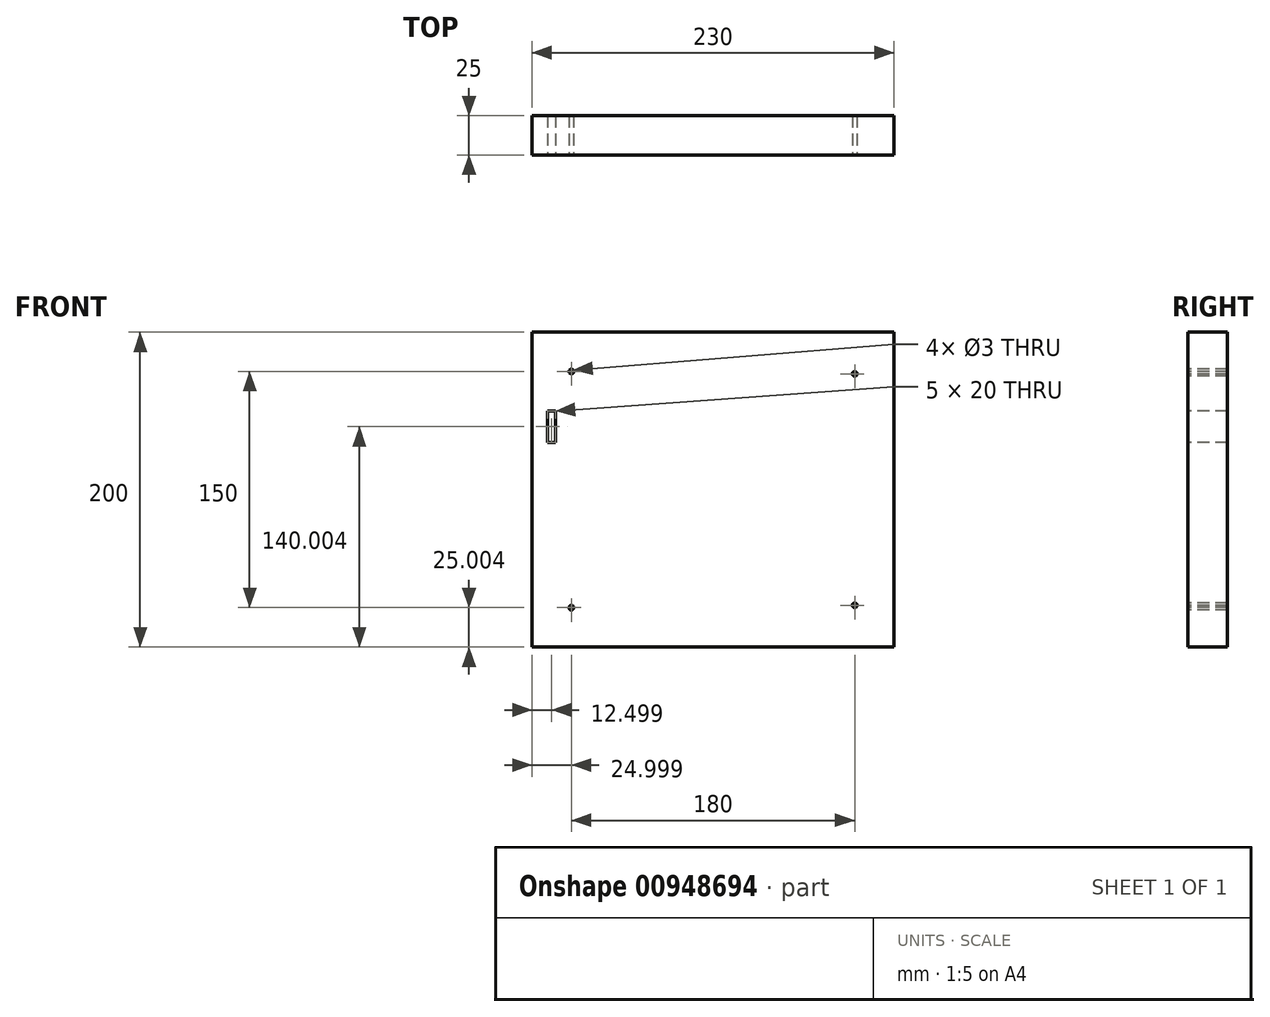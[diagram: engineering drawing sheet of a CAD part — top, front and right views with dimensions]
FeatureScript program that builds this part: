
annotation { "Feature Type Name" : "Feature", "Feature Type Description" : "" }
export const myFeature = defineFeature(function(context is Context, id is Id, definition is map)
    precondition{}
    {
        {
            var Q0;
            Q0=qCreatedBy(makeId("Front.planeOp"),FACE);
            var sketch = newSketch(context, id + "F0", { "sketchPlane" : qUnion([Q0])});
            skLineSegment(sketch, "E0.bottom", {"start": v(-284.04, -13.97) * mm, "end": v(-54.04, -13.97) * mm});
            skLineSegment(sketch, "E0.top", {"start": v(-284.04, -213.97) * mm, "end": v(-54.04, -213.97) * mm});
            skLineSegment(sketch, "E0.left", {"start": v(-284.04, -13.97) * mm, "end": v(-284.04, -213.97) * mm});
            skLineSegment(sketch, "E0.right", {"start": v(-54.04, -13.97) * mm, "end": v(-54.04, -213.97) * mm});
            skSolve(sketch);
        }
        {
            var Q0;
            Q0 = qSketchRegion(id + "F0", true);
            extrude(context, id + "F1", {"entities" : qUnion([Q0]), "depth" : 25 * mm, "offsetDistance" : 25 * mm});
        }
        {
            var Q0;
            Q0=makeQuery(id+"F1.opExtrude","CAP_FACE",FACE,{"disambiguationData":[OSD([sQuery(id+"F0.wireOp",EDGE,"E0.bottom"),sQuery(id+"F0.wireOp",EDGE,"E0.top"),sQuery(id+"F0.wireOp",EDGE,"E0.left"),sQuery(id+"F0.wireOp",EDGE,"E0.right")])],"isStart":false});
            var sketch = newSketch(context, id + "F2", { "sketchPlane" : qUnion([Q0])});
            skLineSegment(sketch, "E1.bottom", {"start": v(-274.04, -63.97) * mm, "end": v(-269.04, -63.97) * mm});
            skLineSegment(sketch, "E1.top", {"start": v(-274.04, -83.97) * mm, "end": v(-269.04, -83.97) * mm});
            skLineSegment(sketch, "E1.left", {"start": v(-274.04, -63.97) * mm, "end": v(-274.04, -83.97) * mm});
            skLineSegment(sketch, "E1.right", {"start": v(-269.04, -63.97) * mm, "end": v(-269.04, -83.97) * mm});
            skCircle(sketch, "E2", {"center": v(-79.04, -40.47) * mm, "radius": 1.5 * mm});
            skCircle(sketch, "E3", {"center": v(-79.04, -187.47) * mm, "radius": 1.5 * mm});
            skCircle(sketch, "E4", {"center": v(-259.04, -38.97) * mm, "radius": 1.5 * mm});
            skCircle(sketch, "E5", {"center": v(-259.04, -188.97) * mm, "radius": 1.5 * mm});
            skSolve(sketch);
        }
        {
            var Q0;
            Q0 = qSketchRegion(id + "F2", true);
            extrude(context, id + "F3", {"entities" : qUnion([Q0]), "operationType" : NewBodyOperationType.REMOVE, "oppositeDirection" : true, "depth" : 25 * mm, "offsetDistance" : 25 * mm});
        }
        {
            var Q0;
            Q0 = qSketchRegion(id + "F2", true);
            extrude(context, id + "F4", {"entities" : qUnion([Q0]), "operationType" : NewBodyOperationType.REMOVE, "oppositeDirection" : true, "depth" : 25 * mm, "offsetDistance" : 25 * mm});
        }
    });
